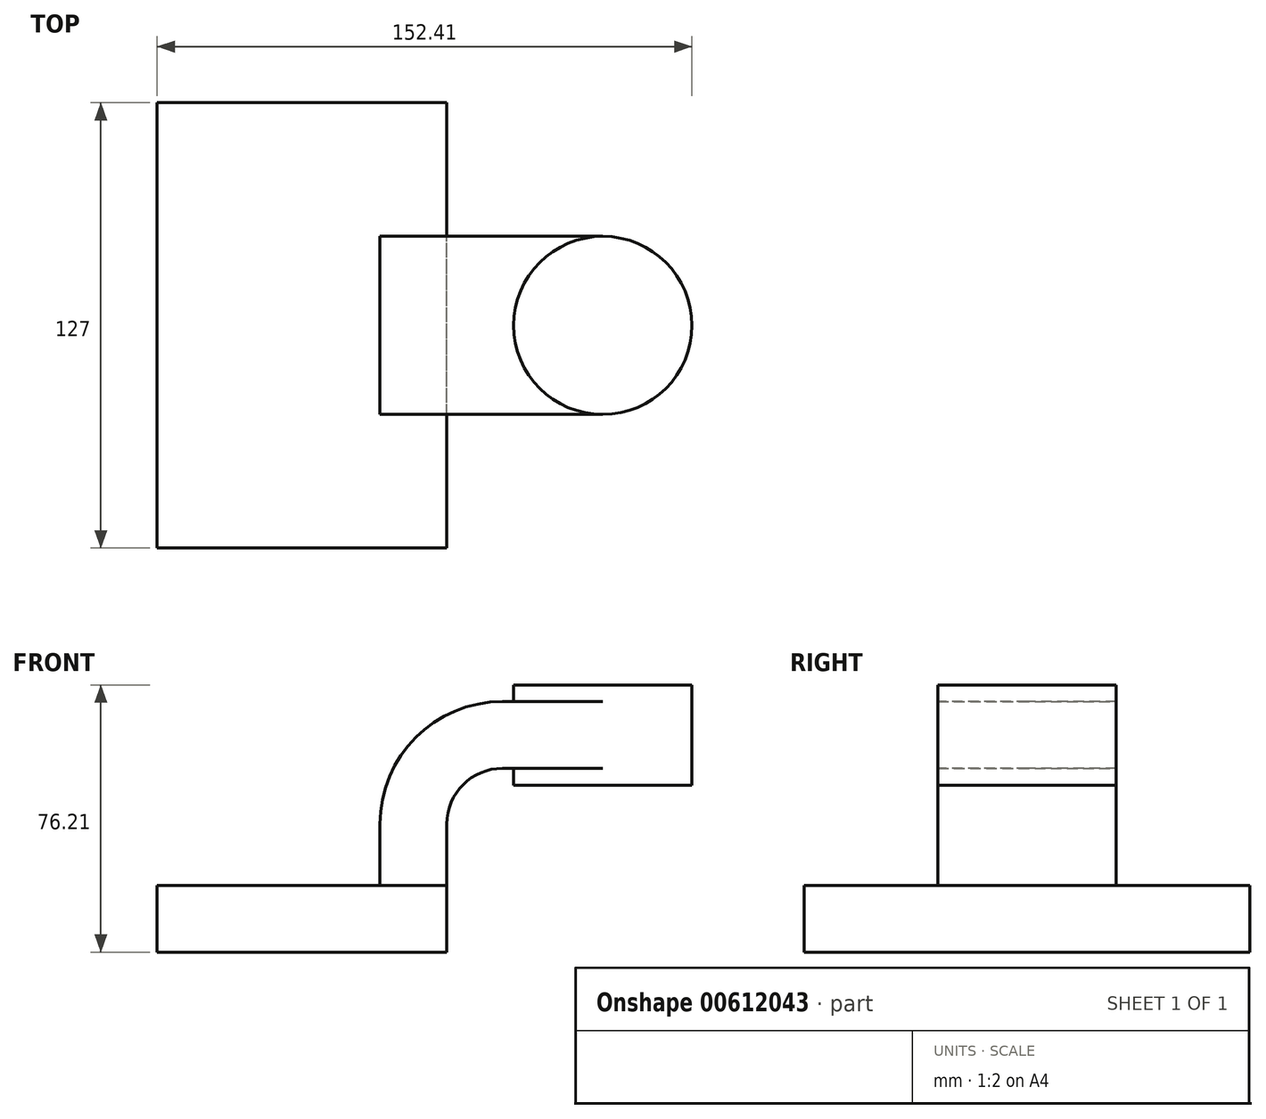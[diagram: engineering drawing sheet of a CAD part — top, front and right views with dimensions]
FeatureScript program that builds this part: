
annotation { "Feature Type Name" : "Feature", "Feature Type Description" : "" }
export const myFeature = defineFeature(function(context is Context, id is Id, definition is map)
    precondition{}
    {
        {
            var Q0;
            Q0=qCreatedBy(makeId("Front.planeOp"),FACE);
            var sketch = newSketch(context, id + "F0", { "sketchPlane" : qUnion([Q0])});
            skLineSegment(sketch, "E0.bottom", {"start": v(41.28, -9.52) * mm, "end": v(-41.28, -9.53) * mm});
            skLineSegment(sketch, "E0.top", {"start": v(41.28, 9.53) * mm, "end": v(-41.28, 9.53) * mm});
            skLineSegment(sketch, "E0.left", {"start": v(41.28, -9.52) * mm, "end": v(41.28, 9.53) * mm});
            skLineSegment(sketch, "E0.right", {"start": v(-41.28, -9.53) * mm, "end": v(-41.28, 9.53) * mm});
            skPoint(sketch, "E0.middle", {"position": v(0, 0) * mm});
            skLineSegment(sketch, "E1", {"start": v(41.28, 9.53) * mm, "end": v(41.28, 27) * mm});
            skLineSegment(sketch, "E2.bottom", {"start": v(60.33, 38.1) * mm, "end": v(111.13, 38.1) * mm});
            skLineSegment(sketch, "E2.top", {"start": v(60.33, 66.68) * mm, "end": v(111.13, 66.68) * mm});
            skLineSegment(sketch, "E2.left", {"start": v(60.33, 38.1) * mm, "end": v(60.33, 66.68) * mm});
            skLineSegment(sketch, "E2.right", {"start": v(111.13, 38.1) * mm, "end": v(111.13, 66.68) * mm});
            skPoint(sketch, "E2.middle", {"position": v(85.73, 52.39) * mm});
            skArc(sketch, "E3", {"start": v(41.27, 27) * mm, "mid": v(45.92, 38.23) * mm, "end": v(57.15, 42.88) * mm});
            skLineSegment(sketch, "E4", {"start": v(57.15, 42.88) * mm, "end": v(101.62, 42.88) * mm});
            skLineSegment(sketch, "E5.0", {"start": v(57.15, 61.93) * mm, "end": v(101.62, 61.93) * mm});
            skArc(sketch, "E5.1", {"start": v(22.23, 27) * mm, "mid": v(32.45, 51.7) * mm, "end": v(57.15, 61.93) * mm});
            skLineSegment(sketch, "E5.2", {"start": v(22.22, 9.53) * mm, "end": v(22.22, 27) * mm});
            skLineSegment(sketch, "E6", {"start": v(85.73, 38.1) * mm, "end": v(85.73, 66.68) * mm});
            skFitSpline(sketch, "E7", {"points": [v(-41.28, 9.53) * mm, v(57.15, 61.93) * mm], "startDerivative": vector(-12.61, 96.42) * mm, "endDerivative": vector(171.45, -11.48) * mm});
            skSolve(sketch);
        }
        {
            var Q0;
            Q0=makeQuery(id+"F0.imprint","IMPRINT",FACE,{"disambiguationData":[TD([[makeQuery(id+"F0.imprint","IMPRINT",EDGE,{"derivedFrom":sQuery(id+"F0.wireOp",EDGE,"E0.bottom")}),-1.0]])]});
            extrude(context, id + "F1", {"entities" : qUnion([Q0]), "endBound" : BoundingType.SYMMETRIC, "depth" : 127 * mm, "offsetDistance" : 25.4 * mm});
        }
        {
            var Q0;
            {var subQ1=sQuery(id+"F0.wireOp",EDGE,"E1");Q0=makeQuery(id+"F0.imprint","IMPRINT",FACE,{"disambiguationData":[TD([[makeQuery(id+"F0.imprint","IMPRINT",EDGE,{"derivedFrom":subQ1}),1.0]])]});}
            var Q1;
            {var subQ0=sQuery(id+"F0.wireOp",EDGE,"E4");var subQ1=sQuery(id+"F0.wireOp",EDGE,"E2.left");var subQ2=makeQuery(id+"F0.imprint","INTERSECT",VERTEX,{"derivedFrom":[subQ1,subQ0]});Q1=makeQuery(id+"F0.imprint","IMPRINT",FACE,{"disambiguationData":[TD([[makeQuery(id+"F0.imprint","IMPRINT",EDGE,{"disambiguationData":[TD([[subQ2,-1.0]])],"derivedFrom":subQ1}),-1.0]])]});}
            extrude(context, id + "F2", {"entities" : qUnion([Q0, Q1]), "endBound" : BoundingType.SYMMETRIC, "depth" : 50.8 * mm, "offsetDistance" : 25.4 * mm});
        }
        {
            var Q0;
            Q0=makeQuery(id+"F0.imprint","IMPRINT",FACE,{"disambiguationData":[TD([[makeQuery(id+"F0.imprint","IMPRINT",EDGE,{"derivedFrom":sQuery(id+"F0.wireOp",EDGE,"E5.1")}),1.0]])]});
            extrude(context, id + "F3", {"entities" : qUnion([Q0]), "endBound" : BoundingType.SYMMETRIC, "depth" : 15.88 * mm, "offsetDistance" : 25.4 * mm});
        }
        {
            var Q0;
            {var subQ4=sQuery(id+"F0.wireOp",EDGE,"E2.right");Q0=makeQuery(id+"F0.imprint","IMPRINT",FACE,{"disambiguationData":[TD([[makeQuery(id+"F0.imprint","IMPRINT",EDGE,{"derivedFrom":subQ4}),1.0]])]});}
            var Q1;
            Q1=sQuery(id+"F0.wireOp",EDGE,"E6");
            revolve(context, id + "F4", {"operationType" : NewBodyOperationType.ADD, "entities" : qUnion([Q0]), "axis" : qUnion([Q1]), "revolveType" : RevolveType.FULL});
        }
    });
